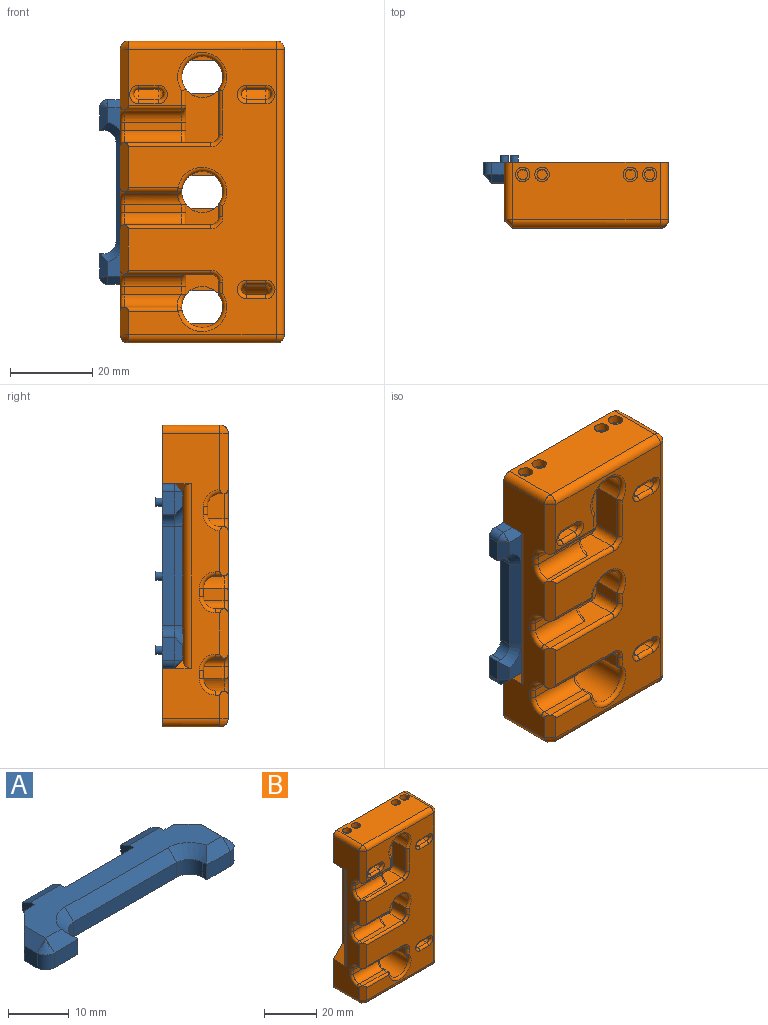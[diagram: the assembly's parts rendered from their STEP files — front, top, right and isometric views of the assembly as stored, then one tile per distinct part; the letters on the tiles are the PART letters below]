
ASSEMBLY  parts=2 mates=1
PART A: 43 faces, bbox 45.1x13.5x6.7 mm
  f0: plane 41x9mm, normal (0,0,1), area 207.7mm2, adj f2,f3,f5,f7,f9,f10,f12,f19
  f1: plane 5.5x3mm, normal (0,-1,0), area 16.5mm2, adj f2,f17,f22,f30
  f2: plane 5.5x2mm, normal (0,-0.71,0.71), area 12.8mm2, adj f0,f1,f27,f30,f36
  f3: plane 3x3mm, normal (-1,0,0), area 7.8mm2, adj f0,f4,f6,f7,f8,f9
  f4: plane 7x2mm, normal (0,0,-1), area 14mm2, adj f3,f5,f8,f9
  f5: plane 3x3mm, normal (1,0,0), area 7.8mm2, adj f0,f4,f6,f7,f8,f9
  f6: plane 7x1mm, normal (0,1,0), area 7mm2, adj f3,f5,f7,f8
  f7: plane 7x2mm, normal (0,0.45,0.89), area 15.7mm2, adj f0,f3,f5,f6
  f8: cylinder r=1mm len=7mm, axis (-1,0,0), area 11mm2, adj f3,f4,f5,f6
  f9: plane 35x5mm, normal (0,1,0), area 133mm2, adj f0,f3,f4,f5,f10,f11,f12,f17
  f10: plane 3x3mm, normal (-1,0,0), area 7.8mm2, adj f0,f9,f11,f13,f14,f19
  f11: plane 7x2mm, normal (0,0,-1), area 14mm2, adj f9,f10,f12,f14
  f12: plane 3x3mm, normal (1,0,0), area 7.8mm2, adj f0,f9,f11,f13,f14,f19
  f13: plane 7x1mm, normal (0,1,0), area 7mm2, adj f10,f12,f14,f19
  f14: cylinder r=1mm len=7mm, axis (-1,0,0), area 11mm2, adj f10,f11,f12,f13
  f15: plane 3x3mm, normal (1,0,0), area 9mm2, adj f17,f21,f23,f24
  f16: plane 3x3mm, normal (-1,0,0), area 9mm2, adj f17,f20,f22,f28
  f17: plane 45x10mm, normal (0,0,-1), area 297.7mm2, adj f1,f9,f15,f16,f18,f20,f21,f22
  f18: plane 5.5x3mm, normal (0,-1,0), area 16.5mm2, adj f17,f23,f26,f31
  f19: plane 7x2mm, normal (0,0.45,0.89), area 15.7mm2, adj f0,f10,f12,f13
  f20: plane 5x5mm, normal (-0.71,0.71,0), area 32.5mm2, adj f0,f9,f16,f17,f28
  f21: plane 5x5mm, normal (0.71,0.71,0), area 32.5mm2, adj f0,f9,f15,f17,f24
  f22: cylinder r=2mm len=3mm, axis (0,0,1), area 9.4mm2, adj f1,f16,f17,f27
  f23: cylinder r=2mm len=3mm, axis (0,0,-1), area 9.4mm2, adj f15,f17,f18,f25
  f24: plane 5x2mm, normal (0.71,0,0.71), area 11.3mm2, adj f0,f15,f21,f25
  f25: cone r=2mm half-angle=45deg, axis (0,0,-1), area 4.4mm2, adj f23,f24,f26
  f26: plane 5.5x2mm, normal (0,-0.71,0.71), area 12.8mm2, adj f0,f18,f25,f31,f34
  f27: cone r=2mm half-angle=45deg, axis (0,0,-1), area 4.4mm2, adj f2,f22,f28
  f28: plane 5x2mm, normal (-0.71,0,0.71), area 11.3mm2, adj f0,f16,f20,f27
  f29: plane 24x3mm, normal (0,-1,0), area 72mm2, adj f17,f32,f33,f35
  f30: plane 3.21x1.09mm, normal (1,0,0), area 3mm2, adj f1,f2,f17,f33,f36
  f31: plane 3.21x1.09mm, normal (-1,0,0), area 3mm2, adj f17,f18,f26,f32,f34
  f32: cylinder r=3mm len=3mm, axis (0,0,1), area 14.1mm2, adj f17,f29,f31,f34
  f33: cylinder r=3mm len=3mm, axis (0,0,-1), area 14.1mm2, adj f17,f29,f30,f36
  f34: cone r=5mm half-angle=45deg, axis (0,0,1), area 17.7mm2, adj f0,f26,f31,f32,f35
  f35: plane 24x2mm, normal (0,-0.71,0.71), area 67.9mm2, adj f0,f29,f34,f36
  f36: cone r=5mm half-angle=45deg, axis (0,0,1), area 17.7mm2, adj f0,f2,f30,f33,f35
  f37: cylinder r=1mm len=2mm, axis (0,0,1), area 10.1mm2, adj f17,f38
  f38: plane 2x2mm, normal (0,0,-1), area 3.1mm2, adj f37
  f39: cylinder r=1mm len=2mm, axis (0,0,1), area 10.1mm2, adj f17,f40
  f40: plane 2x2mm, normal (0,0,-1), area 3.1mm2, adj f39
  f41: cylinder r=1mm len=2mm, axis (0,0,1), area 10.1mm2, adj f17,f42
  f42: plane 2x2mm, normal (0,0,-1), area 3.1mm2, adj f41
PART B: 185 faces, bbox 40.8x17.9x74.4 mm
  f0: plane 35x5mm, normal (-1,0,0), area 133mm2, adj f23,f102,f103,f104,f105,f106,f107,f109
  f1: plane 69.52x14mm, normal (-1,0,0), area 538.9mm2, adj f23,f103,f104,f113,f121,f122,f123,f125
  f2: plane 69.52x36mm, normal (0,-1,0), area 1480.6mm2, adj f114,f117,f120,f123,f125,f127,f128,f129
  f3: cylinder r=5mm len=15mm, axis (0,1,0), area 346.3mm2, adj f7,f14,f15,f17,f22,f23,f31,f32
  f4: cylinder r=5mm len=15mm, axis (0,1,0), area 346.3mm2, adj f5,f12,f13,f18,f20,f23,f25,f26
  f5: plane 5x2.35mm, normal (1,0,0), area 6.2mm2, adj f4,f25,f27,f140,f141
  f6: plane 13x7mm, normal (1,0,0), area 50.7mm2, adj f11,f28,f30,f134,f136,f137,f138,f139
  f7: plane 5x2.35mm, normal (1,0,0), area 6.2mm2, adj f3,f31,f33,f150,f151
  f8: plane 69.52x14mm, normal (1,0,0), area 973.3mm2, adj f23,f115,f117,f118
  f9: plane 36x14mm, normal (0,0,1), area 465.5mm2, adj f23,f56,f58,f60,f62,f113,f114,f115
  f10: plane 36x14mm, normal (0,0,-1), area 484.8mm2, adj f23,f50,f52,f118,f120,f121
  f11: cylinder r=5mm len=15mm, axis (0,1,0), area 367.7mm2, adj f6,f16,f19,f21,f23,f24,f28,f29
  f12: plane 6x1mm, normal (0,-1,0), area 4.1mm2, adj f4,f18
  f13: plane 6x1mm, normal (0,-1,0), area 4.1mm2, adj f4,f20
  f14: plane 6x1mm, normal (0,-1,0), area 4.1mm2, adj f3,f17
  f15: plane 6x1mm, normal (0,-1,0), area 4.1mm2, adj f3,f22
  f16: plane 6x1mm, normal (0,-1,0), area 4.1mm2, adj f11,f19
  f17: plane 6x3mm, normal (0,0,-1), area 18mm2, adj f3,f14,f23
  f18: plane 6x3mm, normal (0,0,-1), area 18mm2, adj f4,f12,f23
  f19: plane 6x3mm, normal (0,0,-1), area 18mm2, adj f11,f16,f23
  f20: plane 6x3mm, normal (0,0,1), area 18mm2, adj f4,f13,f23
  f21: plane 6x3mm, normal (0,0,1), area 18mm2, adj f11,f23,f24
  f22: plane 6x3mm, normal (0,0,1), area 18mm2, adj f3,f15,f23
  f23: plane 73.52x40mm, normal (0,1,0), area 2526.3mm2, adj f0,f1,f3,f4,f8,f9,f10,f11
  f24: plane 6x1mm, normal (0,-1,0), area 4.1mm2, adj f11,f21
  f25: plane 8x5mm, normal (0,-1,0), area 28mm2, adj f4,f5,f26,f27,f42
  f26: plane 7x3mm, normal (-1,0,0), area 21mm2, adj f4,f25,f42,f147
  f27: plane 21.28x7.28mm, normal (0,0,1), area 73mm2, adj f5,f25,f42,f47,f140,f149,f164
  f28: plane 13x8mm, normal (0,-1,0), area 92mm2, adj f6,f11,f29,f30,f41
  f29: plane 11x7mm, normal (-1,0,0), area 77mm2, adj f11,f28,f41,f131
  f30: plane 21.64x7.28mm, normal (0,0,1), area 58.2mm2, adj f6,f28,f41,f43,f128,f129,f139,f184
  f31: plane 8x5mm, normal (0,-1,0), area 28mm2, adj f3,f7,f32,f33,f40
  f32: plane 7x3mm, normal (-1,0,0), area 21mm2, adj f3,f31,f40,f159
  f33: plane 21.28x7.28mm, normal (0,0,-1), area 73mm2, adj f7,f31,f40,f46,f150,f156,f165
  f34: plane 14x2mm, normal (0,-1,0), area 28mm2, adj f45,f46,f151,f152,f167
  f35: plane 13.08x2mm, normal (0,0,1), area 26.2mm2, adj f45,f153,f154,f169
  f36: plane 14x2mm, normal (0,-1,0), area 28mm2, adj f43,f44,f138,f183
  f37: plane 14.37x1mm, normal (0,0,-1), area 14.2mm2, adj f44,f125,f133,f136,f182
  f38: plane 14x2mm, normal (0,-1,0), area 28mm2, adj f47,f48,f141,f142,f162
  f39: plane 13.08x2mm, normal (0,0,-1), area 26.2mm2, adj f48,f143,f144,f160
  f40: cylinder r=2mm len=7mm, axis (0,-1,0), area 22mm2, adj f31,f32,f33,f158
  f41: cylinder r=2mm len=7mm, axis (0,-1,0), area 22mm2, adj f28,f29,f30,f130
  f42: cylinder r=2mm len=7mm, axis (0,1,0), area 22mm2, adj f25,f26,f27,f148
  f43: cylinder r=3mm len=14mm, axis (-1,0,0), area 66mm2, adj f30,f36,f139,f184
  f44: cylinder r=3mm len=14mm, axis (1,0,0), area 66mm2, adj f36,f37,f137,f182
  f45: cylinder r=3mm len=13.8mm, axis (-1,0,0), area 63.4mm2, adj f34,f35,f152,f168
  f46: cylinder r=3mm len=14mm, axis (1,0,0), area 66mm2, adj f33,f34,f150,f166
  f47: cylinder r=3mm len=14mm, axis (-1,0,0), area 66mm2, adj f27,f38,f140,f163
  f48: cylinder r=3mm len=13.8mm, axis (1,0,0), area 63.4mm2, adj f38,f39,f142,f161
  f49: plane 3.5x3.5mm, normal (0,0,-1), area 4.7mm2, adj f50,f53
  f50: cylinder r=1.75mm len=3.5mm, axis (0,0,-1), area 22mm2, adj f10,f49
  f51: plane 3.5x3.5mm, normal (0,0,-1), area 4.7mm2, adj f52,f54
  f52: cylinder r=1.75mm len=3.5mm, axis (0,0,-1), area 22mm2, adj f10,f51
  f53: cylinder r=1.25mm len=6mm, axis (0,0,-1), area 47.1mm2, adj f49,f75,f82
  f54: cylinder r=1.25mm len=6mm, axis (0,0,-1), area 47.1mm2, adj f51,f75,f80
  f55: plane 3.5x3.5mm, normal (0,0,1), area 4.7mm2, adj f56,f65
  f56: cylinder r=1.75mm len=3.5mm, axis (0,0,1), area 22mm2, adj f9,f55
  f57: plane 3.5x3.5mm, normal (0,0,1), area 4.7mm2, adj f58,f67
  f58: cylinder r=1.75mm len=3.5mm, axis (0,0,1), area 22mm2, adj f9,f57
  f59: plane 3.5x3.5mm, normal (0,0,1), area 4.7mm2, adj f60,f71
  f60: cylinder r=1.75mm len=3.5mm, axis (0,0,1), area 22mm2, adj f9,f59
  f61: plane 3.5x3.5mm, normal (0,0,1), area 4.7mm2, adj f62,f73
  f62: cylinder r=1.75mm len=3.5mm, axis (0,0,1), area 22mm2, adj f9,f61
  f63: plane 2.56x2.45mm, normal (0,0,1), area 4.8mm2, adj f64,f65,f89,f90
  f64: cylinder r=1.25mm len=4.77mm, axis (0,0,1), area 3.4mm2, adj f63,f65,f90
  f65: cylinder r=1.25mm len=6mm, axis (0,0,1), area 30.3mm2, adj f55,f63,f64,f84,f89,f90
  f66: plane 2.56x2.45mm, normal (0,0,1), area 4.8mm2, adj f67,f68,f98,f101
  f67: cylinder r=1.25mm len=6mm, axis (0,0,1), area 30.3mm2, adj f57,f66,f68,f93,f98,f101
  f68: cylinder r=1.25mm len=4.77mm, axis (0,0,1), area 3.4mm2, adj f66,f67,f98
  f69: plane 2.56x2.45mm, normal (0,0,1), area 4.8mm2, adj f70,f71,f100,f101
  f70: cylinder r=1.25mm len=3.44mm, axis (0,0,1), area 2.2mm2, adj f69,f71,f101
  f71: cylinder r=1.25mm len=6mm, axis (0,0,1), area 30.5mm2, adj f59,f69,f70,f93,f100,f101
  f72: plane 2.56x2.45mm, normal (0,0,1), area 4.8mm2, adj f73,f74,f89,f92
  f73: cylinder r=1.25mm len=6mm, axis (0,0,1), area 30.5mm2, adj f61,f72,f74,f84,f89,f92
  f74: cylinder r=1.25mm len=3.44mm, axis (0,0,1), area 2.2mm2, adj f72,f73,f89
  f75: plane 4.7x2.5mm, normal (0,0,1), area 6.8mm2, adj f53,f54,f81,f83
  f76: cylinder r=1.25mm len=7mm, axis (0,1,0), area 27.5mm2, adj f77,f79,f80,f178
  f77: plane 7x4.7mm, normal (0,0,-1), area 32.9mm2, adj f76,f78,f81,f179
  f78: cylinder r=1.25mm len=7mm, axis (0,1,0), area 27.5mm2, adj f77,f79,f82,f181
  f79: plane 7x4.7mm, normal (0,0,1), area 32.9mm2, adj f76,f78,f83,f180
  f80: torus R=5mm, axis (-1,0,0), area 30.8mm2, adj f54,f76,f81,f83
  f81: cylinder r=6.25mm len=6.25mm, axis (-1,0,0), area 46.1mm2, adj f75,f77,f80,f82
  f82: torus R=5mm, axis (-1,0,0), area 30.8mm2, adj f53,f78,f81,f83
  f83: cylinder r=3.75mm len=4.7mm, axis (-1,0,0), area 27.7mm2, adj f75,f79,f80,f82
  f84: plane 4.7x2.5mm, normal (0,0,-1), area 6.8mm2, adj f65,f73,f89,f91
  f85: plane 11.77x4.7mm, normal (0,0,-1), area 55.3mm2, adj f86,f88,f89,f175
  f86: cylinder r=1.25mm len=11.77mm, axis (0,1,0), area 46.2mm2, adj f85,f87,f90,f177
  f87: plane 11.77x4.7mm, normal (0,0,1), area 55.3mm2, adj f86,f88,f91,f176
  f88: cylinder r=1.25mm len=11.77mm, axis (0,1,0), area 46.2mm2, adj f85,f87,f92,f174
  f89: cylinder r=6.07mm len=8.52mm, axis (1,0,0), area 34.1mm2, adj f63,f65,f72,f73,f74,f84,f85,f90
  f90: bspline ~11.02x5.29mm, area 31.1mm2, adj f63,f64,f65,f86,f89,f91
  f91: cylinder r=7.86mm len=11.02mm, axis (1,0,0), area 58mm2, adj f84,f87,f90,f92
  f92: bspline ~11.02x5.29mm, area 31.1mm2, adj f72,f73,f88,f89,f91
  f93: plane 4.7x2.5mm, normal (0,0,-1), area 6.8mm2, adj f67,f71,f99,f101
  f94: cylinder r=1.25mm len=11.77mm, axis (0,1,0), area 46.2mm2, adj f95,f97,f98,f170
  f95: plane 11.77x4.7mm, normal (0,0,1), area 55.3mm2, adj f94,f96,f99,f171
  f96: cylinder r=1.25mm len=11.77mm, axis (0,1,0), area 46.2mm2, adj f95,f97,f100,f173
  f97: plane 11.77x4.7mm, normal (0,0,-1), area 55.3mm2, adj f94,f96,f101,f172
  f98: bspline ~11.02x5.29mm, area 31.1mm2, adj f66,f67,f68,f94,f99,f101
  f99: cylinder r=7.86mm len=11.02mm, axis (1,0,0), area 58mm2, adj f93,f95,f98,f100
  f100: bspline ~11.02x5.29mm, area 31.1mm2, adj f69,f71,f96,f99,f101
  f101: cylinder r=6.07mm len=8.52mm, axis (1,0,0), area 34.1mm2, adj f66,f67,f69,f70,f71,f93,f97,f98
  f102: plane 41x8mm, normal (0,1,0), area 184mm2, adj f0,f103,f104,f106,f107,f108,f109,f110
  f103: plane 7.84x5.84mm, normal (-0.71,0,0.71), area 36.6mm2, adj f0,f1,f23,f102,f122
  f104: plane 7.84x5.84mm, normal (-0.71,0,-0.71), area 36.6mm2, adj f0,f1,f23,f102,f122
  f105: plane 7x5mm, normal (0,-1,0), area 35mm2, adj f0,f106,f107,f108
  f106: plane 5x3mm, normal (0,0,1), area 15mm2, adj f0,f102,f105,f108
  f107: plane 5x3mm, normal (0,0,-1), area 15mm2, adj f0,f102,f105,f108
  f108: plane 7x3mm, normal (-1,0,0), area 21mm2, adj f102,f105,f106,f107
  f109: plane 5x3mm, normal (0,0,1), area 15mm2, adj f0,f102,f111,f112
  f110: plane 5x3mm, normal (0,0,-1), area 15mm2, adj f0,f102,f111,f112
  f111: plane 7x5mm, normal (0,-1,0), area 35mm2, adj f0,f109,f110,f112
  f112: plane 7x3mm, normal (-1,0,0), area 21mm2, adj f102,f109,f110,f111
  f113: cylinder r=2mm len=14mm, axis (0,-1,0), area 44mm2, adj f1,f9,f23,f126
  f114: cylinder r=2mm len=36mm, axis (1,0,0), area 113.1mm2, adj f2,f9,f116,f126
  f115: cylinder r=2mm len=14mm, axis (0,1,0), area 44mm2, adj f8,f9,f23,f116
  f116: sphere r=2mm, area 6.3mm2, adj f114,f115,f117
  f117: cylinder r=2mm len=69.52mm, axis (0,0,-1), area 218.4mm2, adj f2,f8,f116,f119
  f118: cylinder r=2mm len=14mm, axis (0,-1,0), area 44mm2, adj f8,f10,f23,f119
  f119: sphere r=2mm, area 6.3mm2, adj f117,f118,f120
  f120: cylinder r=2mm len=36mm, axis (-1,0,0), area 113.1mm2, adj f2,f10,f119,f124
  f121: cylinder r=2mm len=14mm, axis (0,1,0), area 44mm2, adj f1,f10,f23,f124
  f122: cylinder r=2mm len=45mm, axis (0,0,1), area 135.1mm2, adj f1,f102,f103,f104
  f123: plane 7.18x2.42mm, normal (-0.71,-0.71,0), area 18.5mm2, adj f1,f2,f124,f153,f169
  f124: bspline ~2x2mm, area 3mm2, adj f120,f121,f123
  f125: plane 15.18x2.42mm, normal (-0.71,-0.71,0), area 41.2mm2, adj f1,f2,f37,f126,f133,f182
  f126: bspline ~2x2mm, area 3mm2, adj f113,f114,f125
  f127: plane 12.42x2.42mm, normal (-0.71,-0.71,0), area 32.7mm2, adj f1,f2,f149,f156,f164,f165
  f128: plane 12.42x2.42mm, normal (-0.71,-0.71,0), area 32.8mm2, adj f1,f2,f30,f129,f144,f160,f184
  f129: cylinder r=1mm len=21mm, axis (-1,0,0), area 32.2mm2, adj f2,f30,f128,f130
  f130: torus R=3mm, axis (0,-1,0), area 5.8mm2, adj f2,f41,f129,f131
  f131: cylinder r=1mm len=11mm, axis (0,0,-1), area 17mm2, adj f2,f29,f130,f132
  f132: torus R=6mm, axis (0,-1,0), area 36.8mm2, adj f2,f11,f131,f134
  f133: cylinder r=1mm len=14mm, axis (1,0,0), area 21.2mm2, adj f2,f37,f125,f135
  f134: cylinder r=1mm len=4mm, axis (0,0,1), area 6mm2, adj f2,f6,f132,f135
  f135: sphere r=1mm, area 1.6mm2, adj f133,f134,f136
  f136: cylinder r=1mm len=1mm, axis (0,1,0), area 1.6mm2, adj f6,f37,f135,f137
  f137: torus R=4mm, axis (-1,0,0), area 8.3mm2, adj f6,f44,f136,f138
  f138: cylinder r=1mm len=2mm, axis (0,0,-1), area 3.1mm2, adj f6,f36,f137,f139
  f139: torus R=4mm, axis (-1,0,0), area 6.3mm2, adj f6,f30,f43,f138
  f140: torus R=4mm, axis (1,0,0), area 6.3mm2, adj f5,f27,f47,f141
  f141: cylinder r=1mm len=2.01mm, axis (0,0,-1), area 3mm2, adj f4,f5,f38,f140,f142
  f142: bspline ~4.79x4.24mm, area 8.6mm2, adj f4,f38,f48,f141,f143
  f143: cylinder r=1mm len=2mm, axis (0,1,0), area 2.8mm2, adj f4,f39,f142,f145
  f144: cylinder r=1mm len=13.08mm, axis (1,0,0), area 19.8mm2, adj f2,f39,f128,f145
  f145: sphere r=1mm, area 1.4mm2, adj f143,f144,f146
  f146: torus R=6mm, axis (0,-1,0), area 30.2mm2, adj f2,f4,f145,f147
  f147: cylinder r=1mm len=3mm, axis (0,0,-1), area 4.5mm2, adj f2,f26,f146,f148
  f148: torus R=3mm, axis (0,-1,0), area 5.8mm2, adj f2,f42,f147,f149
  f149: cylinder r=1mm len=21mm, axis (-1,0,0), area 32.2mm2, adj f2,f27,f127,f148
  f150: torus R=4mm, axis (1,0,0), area 6.3mm2, adj f7,f33,f46,f151
  f151: cylinder r=1mm len=2.01mm, axis (0,0,-1), area 3mm2, adj f3,f7,f34,f150,f152
  f152: bspline ~4.79x4.24mm, area 8.6mm2, adj f3,f34,f45,f151,f154
  f153: cylinder r=1mm len=13.08mm, axis (-1,0,0), area 19.8mm2, adj f2,f35,f123,f155
  f154: cylinder r=1mm len=2mm, axis (0,1,0), area 2.8mm2, adj f3,f35,f152,f155
  f155: sphere r=1mm, area 1.4mm2, adj f153,f154,f157
  f156: cylinder r=1mm len=21mm, axis (1,0,0), area 32.2mm2, adj f2,f33,f127,f158
  f157: torus R=6mm, axis (0,-1,0), area 30.2mm2, adj f2,f3,f155,f159
  f158: torus R=3mm, axis (0,-1,0), area 5.8mm2, adj f2,f40,f156,f159
  f159: cylinder r=1mm len=3mm, axis (0,0,-1), area 4.5mm2, adj f2,f32,f157,f158
  f160: cylinder r=1mm len=2mm, axis (0,-1,0), area 2.4mm2, adj f1,f39,f128,f161
  f161: torus R=4mm, axis (1,0,0), area 8.3mm2, adj f1,f48,f160,f162
  f162: cylinder r=1mm len=2mm, axis (0,0,1), area 3.1mm2, adj f1,f38,f161,f163
  f163: torus R=4mm, axis (1,0,0), area 8.3mm2, adj f1,f47,f162,f164
  f164: cylinder r=1mm len=2mm, axis (0,1,0), area 2.4mm2, adj f1,f27,f127,f163
  f165: cylinder r=1mm len=2mm, axis (0,-1,0), area 2.4mm2, adj f1,f33,f127,f166
  f166: torus R=4mm, axis (1,0,0), area 8.3mm2, adj f1,f46,f165,f167
  f167: cylinder r=1mm len=2mm, axis (0,0,1), area 3.1mm2, adj f1,f34,f166,f168
  f168: torus R=4mm, axis (1,0,0), area 8.3mm2, adj f1,f45,f167,f169
  f169: cylinder r=1mm len=2mm, axis (0,1,0), area 2.4mm2, adj f1,f35,f123,f168
  f170: torus R=2.25mm, axis (0,-1,0), area 8mm2, adj f2,f94,f171,f172
  f171: cylinder r=1mm len=4.7mm, axis (1,0,0), area 7.4mm2, adj f2,f95,f170,f173
  f172: cylinder r=1mm len=4.7mm, axis (-1,0,0), area 7.4mm2, adj f2,f97,f170,f173
  f173: torus R=2.25mm, axis (0,-1,0), area 8mm2, adj f2,f96,f171,f172
  f174: torus R=2.25mm, axis (0,-1,0), area 8mm2, adj f2,f88,f175,f176
  f175: cylinder r=1mm len=4.7mm, axis (-1,0,0), area 7.4mm2, adj f2,f85,f174,f177
  f176: cylinder r=1mm len=4.7mm, axis (1,0,0), area 7.4mm2, adj f2,f87,f174,f177
  f177: torus R=2.25mm, axis (0,-1,0), area 8mm2, adj f2,f86,f175,f176
  f178: torus R=2.25mm, axis (0,-1,0), area 8mm2, adj f2,f76,f179,f180
  f179: cylinder r=1mm len=4.7mm, axis (-1,0,0), area 7.4mm2, adj f2,f77,f178,f181
  f180: cylinder r=1mm len=4.7mm, axis (1,0,0), area 7.4mm2, adj f2,f79,f178,f181
  f181: torus R=2.25mm, axis (0,-1,0), area 8mm2, adj f2,f78,f179,f180
  f182: torus R=4mm, axis (1,0,0), area 8.8mm2, adj f1,f37,f44,f125,f183
  f183: cylinder r=1mm len=2mm, axis (0,0,1), area 3.1mm2, adj f1,f36,f182,f184
  f184: torus R=4mm, axis (1,0,0), area 8.8mm2, adj f1,f30,f43,f128,f183
PLACE A rot(axis=(0.58,0.58,-0.58),120deg) t=(-9.64,27.75,18.61)mm
PLACE B t=(5.36,24.75,18.61)mm
MATE planar B.f23 <-> A.f17  axis (0,1,0) through (-9.64,27.75,1.11)mm
